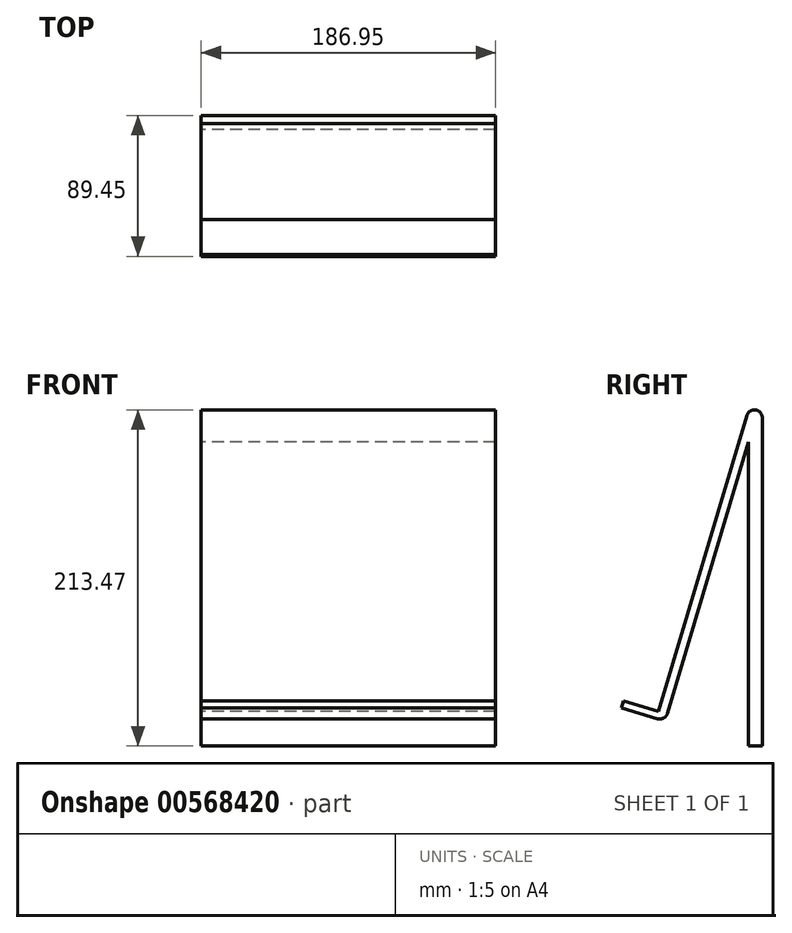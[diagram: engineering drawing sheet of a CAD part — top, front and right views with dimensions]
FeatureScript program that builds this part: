
annotation { "Feature Type Name" : "Feature", "Feature Type Description" : "" }
export const myFeature = defineFeature(function(context is Context, id is Id, definition is map)
    precondition{}
    {
        {
            var Q0;
            Q0=qCreatedBy(makeId("Right.planeOp"),FACE);
            var sketch = newSketch(context, id + "F0", { "sketchPlane" : qUnion([Q0])});
            skLineSegment(sketch, "E0", {"start": v(-26.33, -53.17) * mm, "end": v(30.86, 138.44) * mm});
            skLineSegment(sketch, "E1", {"start": v(30.86, 117.94) * mm, "end": v(30.86, -75.03) * mm});
            skLineSegment(sketch, "E2", {"start": v(30.86, -75.03) * mm, "end": v(39.64, -75.03) * mm});
            skLineSegment(sketch, "E3", {"start": v(39.64, -75.03) * mm, "end": v(39.64, 138.44) * mm});
            skLineSegment(sketch, "E4", {"start": v(-27.62, -57.49) * mm, "end": v(-49.8, -50.86) * mm});
            skLineSegment(sketch, "E5", {"start": v(-49.8, -50.86) * mm, "end": v(-48.52, -46.55) * mm});
            skPoint(sketch, "E6.end.orphan", {"position": v(-27.62, -52.79) * mm});
            skLineSegment(sketch, "E7", {"start": v(-48.52, -46.55) * mm, "end": v(-26.33, -53.17) * mm});
            skLineSegment(sketch, "E8", {"start": v(-27.62, -57.49) * mm, "end": v(-22, -59.16) * mm});
            skLineSegment(sketch, "E9", {"start": v(-22, -59.16) * mm, "end": v(30.86, 117.94) * mm});
            skLineSegment(sketch, "E10", {"start": v(30.86, 138.44) * mm, "end": v(39.64, 138.44) * mm});
            skSolve(sketch);
        }
        {
            var Q0;
            Q0 = qSketchRegion(id + "F0", true);
            extrude(context, id + "F1", {"entities" : qUnion([Q0]), "depth" : 82.3 * mm, "offsetDistance" : 25.4 * mm, "hasSecondDirection" : true, "secondDirectionOppositeDirection" : true, "secondDirectionDepth" : 104.65 * mm});
        }
        {
            var Q0;
            Q0=makeQuery(id+"F1.opExtrude","SWEPT_EDGE",EDGE,{"disambiguationData":[OSD([sQuery(id+"F0.wireOp",EDGE,"E3"),sQuery(id+"F0.wireOp",EDGE,"E10")])]});
            fillet(context, id + "F2", {"entities" : qUnion([Q0]), "radius" : 5.08 * mm, "tangentPropagation" : true, "allowEdgeOverflow" : false});
        }
        {
            var Q0;
            Q0=makeQuery(id+"F1.opExtrude","SWEPT_EDGE",EDGE,{"disambiguationData":[OSD([sQuery(id+"F0.wireOp",EDGE,"E0"),sQuery(id+"F0.wireOp",EDGE,"E10")])]});
            fillet(context, id + "F3", {"entities" : qUnion([Q0]), "radius" : 5.08 * mm, "tangentPropagation" : true, "allowEdgeOverflow" : false});
        }
        {
            var Q0;
            Q0=makeQuery(id+"F1.opExtrude","SWEPT_EDGE",EDGE,{"disambiguationData":[OSD([sQuery(id+"F0.wireOp",EDGE,"E8"),sQuery(id+"F0.wireOp",EDGE,"E9")])]});
            fillet(context, id + "F4", {"entities" : qUnion([Q0]), "radius" : 5.08 * mm, "tangentPropagation" : true, "allowEdgeOverflow" : false});
        }
    });
